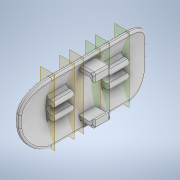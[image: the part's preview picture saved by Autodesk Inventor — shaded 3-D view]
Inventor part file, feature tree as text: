
AUTODESK INVENTOR PART (.ipt)
format: ipt  version: 2021 (Build 250183000, 183)  size: 390,656 bytes
history: native  units: in
note: dims shown in document units (in); Inventor stores cm internally (conversion verified against a paired STEP export)
features: plane x6, extrude x5, sketch x5, fillet x4, projected_geometry x4, chamfer x2
ambient origin geometry x8: Origin, YZ Plane, XZ Plane, XY Plane, X Axis, Y Axis, Z Axis, Center Point
bodies: Solid1 (feature_tree)
feature tree (26):
  extrude  "Extrusion1"  Depth=1.4567in
  fillet  "Fillet2"  Radius=0.2165in
  plane  "Work Plane1"
  plane  "Work Plane3"
  plane  "Work Plane4"
  extrude  "Extrusion2"  Depth=0.1181in
  extrude  "Extrusion3"  Depth=0.0197in
  extrude  "Extrusion4"  Depth=0.1181in
  plane  "Work Plane5"
  plane  "Work Plane6"
  extrude  "Extrusion5"  Depth=0.0591in
  fillet  "Fillet3"  [1 undecoded]
  fillet  "Fillet4"  [1 undecoded]
  chamfer  "Chamfer3"  Distance=3.0709in
  fillet  "Fillet5"  Radius=3.0709in
  chamfer  "Chamfer2"  Distance=3.0709in
  sketch  "Sketch1"  dims[d0=0.2035in d1=1.4567in d2=0.2165in]
  plane  "Work Plane2"
  sketch  "Sketch2"  dims[d3=1.4567in d4=0.1181in]
  projected_geometry  "Projected Loop1"
  sketch  "Sketch3"  dims[d5=3.0709in d6=0.0in d8=0.0197in]
  projected_geometry  "Projected Loop2"
  sketch  "Sketch4"  dims[d9=0.1969in d10=0.1181in]
  projected_geometry  "Projected Loop3"
  sketch  "Sketch6"  dims[d11=0.1575in d12=0.0591in d13=-0.6299in d14=-0.6299in d15=-0.4724in d16=-0.4724in d17=3.0709in d18=0.0in d19=3.0709in d20=0.0in d21=3.0709in d22=0.0in d23=-0.2362in d24=-0.2362in d32=0.7874in d33=0.1181in d34=0.1181in d35=0.1181in d36=0.1181in d37=0.0787in d39=3.0709in d40=0.0in d41=0.4724in d42=0.0787in d43=0.5906in d44=0.0394in d45=0.0394in d49=0.0394in d50=0.0787in d51=45.0deg d52=0.0787in d53=0.0787in d54=45.0deg]
  projected_geometry  "Projected Loop5"
note: 2 required parameter values undecoded (feature->parameter linkage not recoverable at this tier; creation-order binding heuristic only, values carry confidence <= 0.55)
